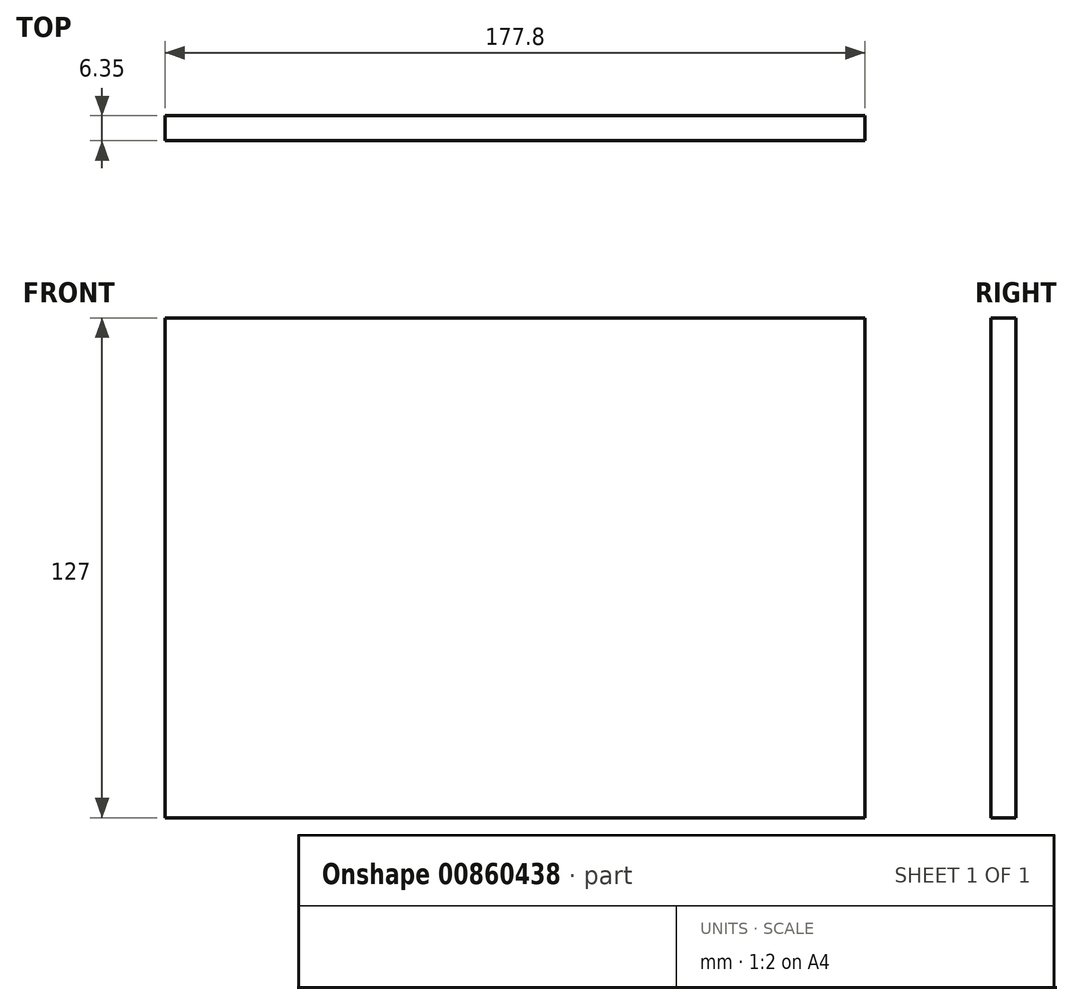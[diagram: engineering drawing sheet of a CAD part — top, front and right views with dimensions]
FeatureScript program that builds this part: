
annotation { "Feature Type Name" : "Feature", "Feature Type Description" : "" }
export const myFeature = defineFeature(function(context is Context, id is Id, definition is map)
    precondition{}
    {
        {
            var Q0;
            Q0=qCreatedBy(makeId("Front.planeOp"),FACE);
            var sketch = newSketch(context, id + "F0", { "sketchPlane" : qUnion([Q0])});
            skLineSegment(sketch, "E0.bottom", {"start": v(-46.21, 56.23) * mm, "end": v(131.59, 56.23) * mm});
            skLineSegment(sketch, "E0.top", {"start": v(-46.21, -70.77) * mm, "end": v(131.59, -70.77) * mm});
            skLineSegment(sketch, "E0.left", {"start": v(-46.21, 56.23) * mm, "end": v(-46.21, -70.77) * mm});
            skLineSegment(sketch, "E0.right", {"start": v(131.59, 56.23) * mm, "end": v(131.59, -70.77) * mm});
            skSolve(sketch);
        }
        {
            var Q0;
            Q0 = qSketchRegion(id + "F0", true);
            extrude(context, id + "F1", {"entities" : qUnion([Q0]), "depth" : 6.35 * mm, "offsetDistance" : 25.4 * mm});
        }
    });
